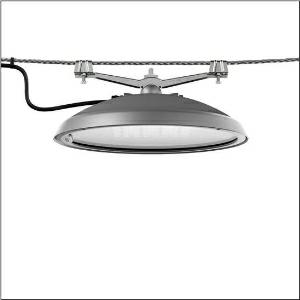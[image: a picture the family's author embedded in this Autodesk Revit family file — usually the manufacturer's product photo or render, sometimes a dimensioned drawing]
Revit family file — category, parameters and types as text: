
# Revit family: dl_r__50_iq_mini___st1_0s_5xa248w31f08he_c7f4
name_source: partatom
category: Lighting Fixtures
units: mm (PartAtom-declared; Revit-internal decimal feet)

## family parameters
Cut with Voids When Loaded = No
Host = Face
Light Source = No
Part Type = Normal
Room Calculation Point = No
Round Connector Dimension = Use Diameter
Shared = No

## types (1)
- --- (1 x LED, 9400 lm, 68.6 W, 3000K)
    Apparent Load = 69 VA
    CIE Flux Codes = 37 72 97 100 100
    Color Rendering = 70
    Color Temperature = 3000K
    Default Elevation = 1800 mm
    Description = DL® 50 iQ mini, catenary luminaire, primary light control with lens, of PMMA, primary optical cover: cover, of toughened safety glass, transparent, light distribution: ST1.0s, light emission: direct distribution, primary light characteristic: symmetric, installation type: suspended mounting, LED, High Power LED, rated luminous flux: 9.400lm, luminous efficacy: 137lm/W, light colour: 730, colour temperature: 3000K, control gear: iQ Street-Remote, control: optimised constant luminous flux control (CLO 2.0), Desk-Remote (wireless, voltage-free reading and setting of iQ features in the workshop via application-optimized NFC function/RFID function), Light-Fading, Smart-Wire, Night-Set, Lumen-Switch, Temp-Guard, Auto-Match, Street-Remote, mains connection: 230..240V, AC, 50/60Hz, start of lifetime: 69W, end of service life: 72W, reduction: 30W, luminaire housing, of diecast aluminium, powder-coated, Siteco® metallic grey (DB 702S), diameter: 500mm, height: 115mm, mounting height: 4..12m, protection rating (complete): IP66, insulation class (complete): insulation class II (safety insulation), certification: CE, ENEC, ENEC+, VDE, impact resistance: IK08, permissible operating ambient temperature for outdoor applications: -25..+40°C, standard-compliant lighting for roads and squares, packaging unit: 1 piece

Light Distribution: ST1.0s
    Height = 124 mm  [stored 0.406824 ft]
    Lamp = 1 x LED
    Lamp Light Flux = 9400 lm
    Lamp Power = 68.6 W
    Lamp count = 1
    Length = 500 mm
    Luminous efficacy = 137 lm/W
    Manufacturer = Siteco
    ModVariant = No
    Model = 5XA248W31F08HE
    Number of Poles = 1
    OnlyDefault = Yes
    Power Factor = 1
    Product Name = DL® 50 iQ mini | ST1.0s
    Product group = catenary luminaire
    ProductGroupID = 6300
    Protection Class = Protection class II
    Protection Degree = IP 66
    RLX_Detail_Level = 1
    RLX_Emergency_Light_Flux = 0 lm
    RLX_Emergency_Type = 0
    RLX_Emergency_Type_DB = No
    RlxData = <blob elided: 123557 chars, md5=070d78d6>
    Socket = socket
    Standby Power = 0 W
    System Light Flux = 9400 lm
    System Power = 69 W
    Type Comments = factory setting: luminous flux: 100 % | dim-lin: 254 | 693 mA
    Type Image = l_1242791.jpg
    URL = http://relux.com
    VarID = @adj_140640
    Voltage = 0 V
    Weight = 0.00 kg
    Width = 0 mm  [stored 0 ft]

note: [stored X ft] marks values corroborated as IEEE doubles in the binary element streams (Revit-internal decimal feet)

## geometry (parser evidence)
native form markers: Blend x4, Sweep x14
no freeform markers — native parametric forms only
